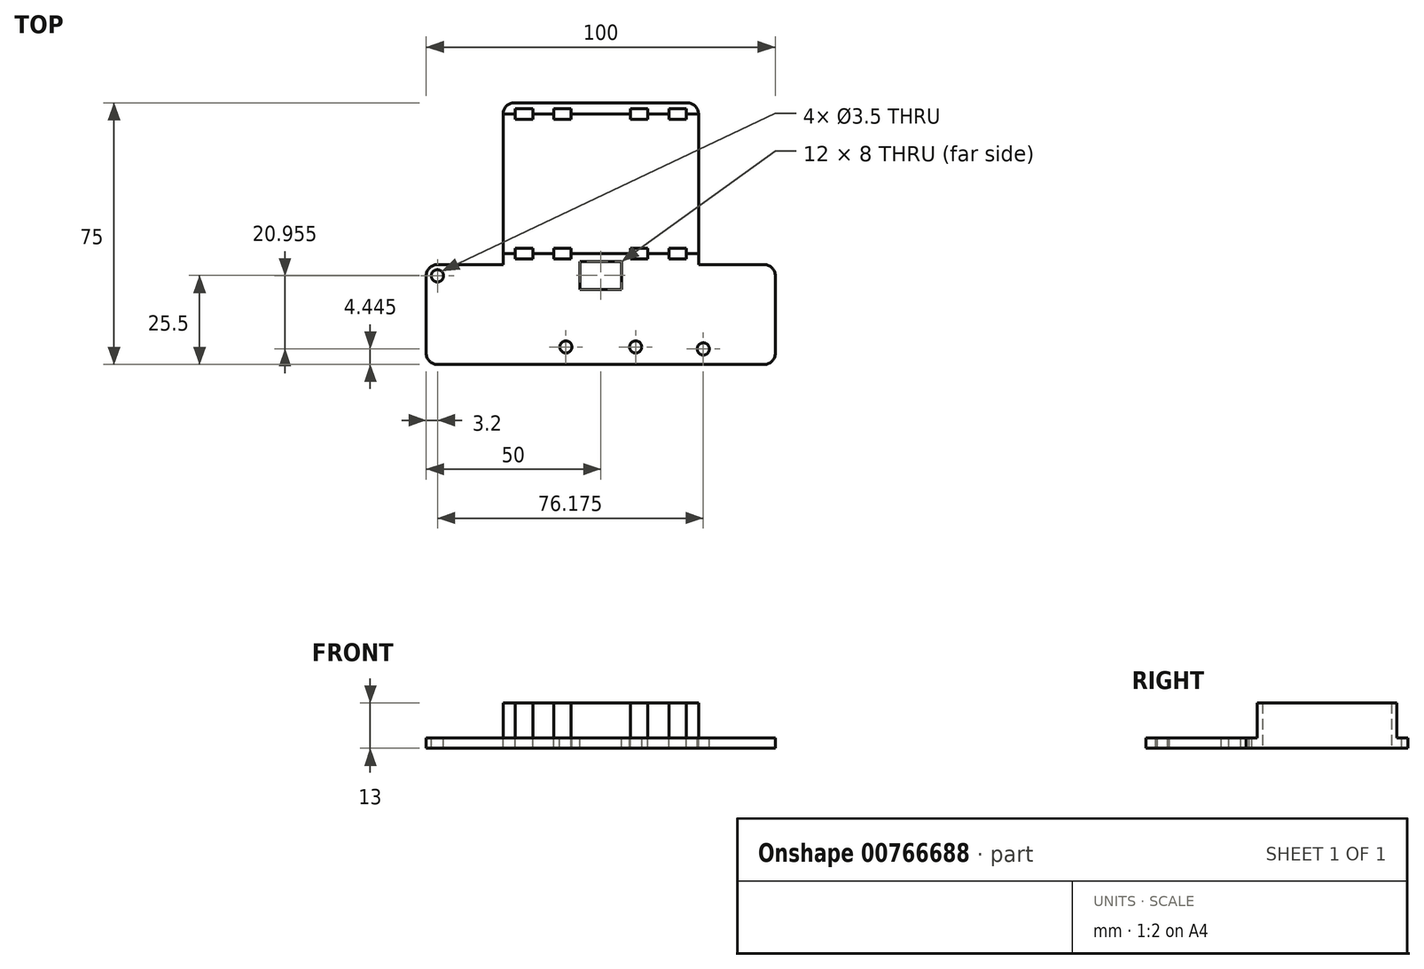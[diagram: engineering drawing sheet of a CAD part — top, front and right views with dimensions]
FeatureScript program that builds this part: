
annotation { "Feature Type Name" : "Feature", "Feature Type Description" : "" }
export const myFeature = defineFeature(function(context is Context, id is Id, definition is map)
    precondition{}
    {
        {
            var Q0;
            Q0=qCreatedBy(makeId("Top.planeOp"),FACE);
            var sketch = newSketch(context, id + "F0", { "sketchPlane" : qUnion([Q0])});
            skLineSegment(sketch, "E0.bottom", {"start": v(-28, -37.5) * mm, "end": v(0, -37.5) * mm});
            skLineSegment(sketch, "E0.top", {"start": v(-28, 37.5) * mm, "end": v(28, 37.5) * mm});
            skPoint(sketch, "E0.middle", {"position": v(0, 0) * mm});
            skCircle(sketch, "E1", {"center": v(-10, -32.5) * mm, "radius": 1.75 * mm});
            skCircle(sketch, "E2", {"center": v(10, -32.5) * mm, "radius": 1.75 * mm});
            skCircle(sketch, "E3", {"center": v(-46.8, -12.1) * mm, "radius": 1.75 * mm});
            skCircle(sketch, "E4", {"center": v(29.38, -33.05) * mm, "radius": 1.75 * mm});
            skLineSegment(sketch, "E5", {"start": v(-28, -37.5) * mm, "end": v(-50, -37.5) * mm});
            skLineSegment(sketch, "E6", {"start": v(28, -37.5) * mm, "end": v(50, -37.5) * mm});
            skLineSegment(sketch, "E7", {"start": v(50, -37.5) * mm, "end": v(50, -8.9) * mm});
            skLineSegment(sketch, "E8", {"start": v(50, -8.9) * mm, "end": v(-50, -8.9) * mm});
            skLineSegment(sketch, "E9", {"start": v(-50, -8.9) * mm, "end": v(-50, -37.5) * mm});
            skLineSegment(sketch, "E10.trimOffspring", {"start": v(28, -8.9) * mm, "end": v(28, 37.5) * mm});
            skLineSegment(sketch, "E11.trimOffspring", {"start": v(-28, -8.9) * mm, "end": v(-28, 14.3) * mm});
            skLineSegment(sketch, "E12", {"start": v(0, -37.5) * mm, "end": v(28, -37.5) * mm});
            skLineSegment(sketch, "E13", {"start": v(-28, 14.3) * mm, "end": v(-28, 37.5) * mm});
            skLineSegment(sketch, "E14", {"start": v(-28, 34.3) * mm, "end": v(28, 34.3) * mm});
            skLineSegment(sketch, "E15", {"start": v(-28, -5.7) * mm, "end": v(28, -5.7) * mm});
            skLineSegment(sketch, "E16", {"start": v(-5, -5.7) * mm, "end": v(-5, 34.3) * mm});
            skLineSegment(sketch, "E17", {"start": v(5, 34.3) * mm, "end": v(5, -5.7) * mm});
            skLineSegment(sketch, "E18.bottom", {"start": v(-19.5, 35.8) * mm, "end": v(-24.5, 35.8) * mm});
            skLineSegment(sketch, "E18.top", {"start": v(-19.5, 32.8) * mm, "end": v(-24.5, 32.8) * mm});
            skLineSegment(sketch, "E18.left", {"start": v(-19.5, 35.8) * mm, "end": v(-19.5, 32.8) * mm});
            skLineSegment(sketch, "E18.right", {"start": v(-24.5, 35.8) * mm, "end": v(-24.5, 32.8) * mm});
            skPoint(sketch, "E18.middle", {"position": v(-22, 34.3) * mm});
            skLineSegment(sketch, "E19.bottom", {"start": v(-13.5, 32.8) * mm, "end": v(-8.5, 32.8) * mm});
            skLineSegment(sketch, "E19.top", {"start": v(-13.5, 35.8) * mm, "end": v(-8.5, 35.8) * mm});
            skLineSegment(sketch, "E19.left", {"start": v(-13.5, 32.8) * mm, "end": v(-13.5, 35.8) * mm});
            skLineSegment(sketch, "E19.right", {"start": v(-8.5, 32.8) * mm, "end": v(-8.5, 35.8) * mm});
            skPoint(sketch, "E19.middle", {"position": v(-11, 34.3) * mm});
            skLineSegment(sketch, "E20.bottom", {"start": v(-19.5, -4.2) * mm, "end": v(-24.5, -4.2) * mm});
            skLineSegment(sketch, "E20.top", {"start": v(-19.5, -7.2) * mm, "end": v(-24.5, -7.2) * mm});
            skLineSegment(sketch, "E20.left", {"start": v(-19.5, -4.2) * mm, "end": v(-19.5, -7.2) * mm});
            skLineSegment(sketch, "E20.right", {"start": v(-24.5, -4.2) * mm, "end": v(-24.5, -7.2) * mm});
            skPoint(sketch, "E20.middle", {"position": v(-22, -5.7) * mm});
            skLineSegment(sketch, "E21.bottom", {"start": v(-13.5, -4.2) * mm, "end": v(-8.5, -4.2) * mm});
            skLineSegment(sketch, "E21.top", {"start": v(-13.5, -7.2) * mm, "end": v(-8.5, -7.2) * mm});
            skLineSegment(sketch, "E21.left", {"start": v(-13.5, -4.2) * mm, "end": v(-13.5, -7.2) * mm});
            skLineSegment(sketch, "E21.right", {"start": v(-8.5, -4.2) * mm, "end": v(-8.5, -7.2) * mm});
            skPoint(sketch, "E21.middle", {"position": v(-11, -5.7) * mm});
            skLineSegment(sketch, "E22.bottom", {"start": v(8.5, 32.8) * mm, "end": v(13.5, 32.8) * mm});
            skLineSegment(sketch, "E22.top", {"start": v(8.5, 35.8) * mm, "end": v(13.5, 35.8) * mm});
            skLineSegment(sketch, "E22.left", {"start": v(8.5, 32.8) * mm, "end": v(8.5, 35.8) * mm});
            skLineSegment(sketch, "E22.right", {"start": v(13.5, 32.8) * mm, "end": v(13.5, 35.8) * mm});
            skPoint(sketch, "E22.middle", {"position": v(11, 34.3) * mm});
            skLineSegment(sketch, "E23.bottom", {"start": v(19.5, 32.8) * mm, "end": v(24.5, 32.8) * mm});
            skLineSegment(sketch, "E23.top", {"start": v(19.5, 35.8) * mm, "end": v(24.5, 35.8) * mm});
            skLineSegment(sketch, "E23.left", {"start": v(19.5, 32.8) * mm, "end": v(19.5, 35.8) * mm});
            skLineSegment(sketch, "E23.right", {"start": v(24.5, 32.8) * mm, "end": v(24.5, 35.8) * mm});
            skPoint(sketch, "E23.middle", {"position": v(22, 34.3) * mm});
            skLineSegment(sketch, "E24.bottom", {"start": v(13.5, -4.2) * mm, "end": v(8.5, -4.2) * mm});
            skLineSegment(sketch, "E24.top", {"start": v(13.5, -7.2) * mm, "end": v(8.5, -7.2) * mm});
            skLineSegment(sketch, "E24.left", {"start": v(13.5, -4.2) * mm, "end": v(13.5, -7.2) * mm});
            skLineSegment(sketch, "E24.right", {"start": v(8.5, -4.2) * mm, "end": v(8.5, -7.2) * mm});
            skPoint(sketch, "E24.middle", {"position": v(11, -5.7) * mm});
            skPoint(sketch, "E24.middle.positionSnap0", {"position": v(11, 32.8) * mm});
            skPoint(sketch, "E24.centerSnap0", {"position": v(11, 32.8) * mm});
            skLineSegment(sketch, "E25.bottom", {"start": v(19.5, -4.2) * mm, "end": v(24.5, -4.2) * mm});
            skLineSegment(sketch, "E25.top", {"start": v(19.5, -7.2) * mm, "end": v(24.5, -7.2) * mm});
            skLineSegment(sketch, "E25.left", {"start": v(19.5, -4.2) * mm, "end": v(19.5, -7.2) * mm});
            skLineSegment(sketch, "E25.right", {"start": v(24.5, -4.2) * mm, "end": v(24.5, -7.2) * mm});
            skPoint(sketch, "E25.middle", {"position": v(22, -5.7) * mm});
            skPoint(sketch, "E25.middle.positionSnap0", {"position": v(22, 32.8) * mm});
            skPoint(sketch, "E25.centerSnap0", {"position": v(22, 32.8) * mm});
            skLineSegment(sketch, "E26.bottom", {"start": v(6, -8) * mm, "end": v(-6, -8) * mm});
            skLineSegment(sketch, "E26.top", {"start": v(6, -16) * mm, "end": v(-6, -16) * mm});
            skLineSegment(sketch, "E26.left", {"start": v(6, -8) * mm, "end": v(6, -16) * mm});
            skLineSegment(sketch, "E26.right", {"start": v(-6, -8) * mm, "end": v(-6, -16) * mm});
            skPoint(sketch, "E26.middle", {"position": v(0, -12) * mm});
            skSolve(sketch);
        }
        {
            var Q0;
            {var subQ0=sQuery(id+"F0.wireOp",EDGE,"E16");Q0=makeQuery(id+"F0.imprint","IMPRINT",FACE,{"disambiguationData":[TD([[makeQuery(id+"F0.imprint","IMPRINT",EDGE,{"derivedFrom":subQ0}),-1.0]])]});}
            var Q1;
            {var subQ3=sQuery(id+"F0.wireOp",EDGE,"E16");Q1=makeQuery(id+"F0.imprint","IMPRINT",FACE,{"disambiguationData":[TD([[makeQuery(id+"F0.imprint","IMPRINT",EDGE,{"derivedFrom":subQ3}),1.0]])]});}
            var Q2;
            {var subQ5=sQuery(id+"F0.wireOp",EDGE,"E17");Q2=makeQuery(id+"F0.imprint","IMPRINT",FACE,{"disambiguationData":[TD([[makeQuery(id+"F0.imprint","IMPRINT",EDGE,{"derivedFrom":subQ5}),1.0]])]});}
            extrude(context, id + "F1", {"entities" : qUnion([Q0, Q1, Q2]), "depth" : 3 * mm, "offsetDistance" : 25 * mm});
        }
        {
            var Q0;
            {var subQ3=sQuery(id+"F0.wireOp",EDGE,"E16");Q0=makeQuery(id+"F0.imprint","IMPRINT",FACE,{"disambiguationData":[TD([[makeQuery(id+"F0.imprint","IMPRINT",EDGE,{"derivedFrom":subQ3}),1.0]])]});}
            var Q1;
            {var subQ5=sQuery(id+"F0.wireOp",EDGE,"E17");Q1=makeQuery(id+"F0.imprint","IMPRINT",FACE,{"disambiguationData":[TD([[makeQuery(id+"F0.imprint","IMPRINT",EDGE,{"derivedFrom":subQ5}),1.0]])]});}
            extrude(context, id + "F2", {"entities" : qUnion([Q0, Q1]), "operationType" : NewBodyOperationType.ADD, "oppositeDirection" : true, "depth" : 10 * mm, "offsetDistance" : 25 * mm});
        }
        {
            var Q0;
            {var subQ0=sQuery(id+"F0.wireOp",EDGE,"E10.trimOffspring");Q0=makeQuery(id+"F2.boolean.opBoolean","MERGE",FACE,{"derivedFrom":[makeQuery(id+"F1.opExtrude","SWEPT_FACE",FACE,{"disambiguationData":[OSD([subQ0])]}),makeQuery(id+"F2.opExtrude","SWEPT_FACE",FACE,{"disambiguationData":[OSD([subQ0])]})]});}
            var sketch = newSketch(context, id + "F3", { "sketchPlane" : qUnion([Q0])});
            skPoint(sketch, "E27.0", {"position": v(14.3, 0) * mm});
            skCircle(sketch, "E28", {"center": v(14.3, -17.5) * mm, "radius": 17.5 * mm});
            skSolve(sketch);
        }
        {
            var Q0;
            {var subQ0=sQuery(id+"F3.wireOp",EDGE,"E28");var subQ1=makeQuery(id+"F2.opExtrude","CAP_EDGE",EDGE,{"disambiguationData":[OSD([sQuery(id+"F0.wireOp",EDGE,"E10.trimOffspring")])],"isStart":false});var subQ2=makeQuery(id+"F3.imprint","INTERSECT",VERTEX,{"disambiguationData":[OD(0.0)],"derivedFrom":[subQ1,subQ0]});Q0=makeQuery(id+"F3.imprint","IMPRINT",FACE,{"disambiguationData":[TD([[makeQuery(id+"F3.imprint","IMPRINT",EDGE,{"disambiguationData":[TD([[subQ2,-1.0]])],"derivedFrom":subQ0}),1.0]])]});}
            var Q1;
            {var subQ0=sQuery(id+"F0.wireOp",EDGE,"E13");var subQ1=sQuery(id+"F0.wireOp",EDGE,"E11.trimOffspring");Q1=makeQuery(id+"F2.boolean.opBoolean","MERGE",FACE,{"derivedFrom":[makeQuery(id+"F1.opExtrude","SWEPT_FACE",FACE,{"disambiguationData":[OSD([subQ1,subQ0])]}),makeQuery(id+"F2.opExtrude","SWEPT_FACE",FACE,{"disambiguationData":[OSD([subQ1,subQ0])]})]});}
            extrude(context, id + "F4", {"entities" : qUnion([Q0]), "operationType" : NewBodyOperationType.REMOVE, "endBound" : BoundingType.UP_TO_SURFACE, "oppositeDirection" : true, "depth" : 25 * mm, "endBoundEntityFace" : qUnion([Q1]), "offsetDistance" : 25 * mm});
        }
        {
            var Q0;
            {var subQ0=sQuery(id+"F0.wireOp",EDGE,"E16");Q0=makeQuery(id+"F0.imprint","IMPRINT",FACE,{"disambiguationData":[TD([[makeQuery(id+"F0.imprint","IMPRINT",EDGE,{"derivedFrom":subQ0}),-1.0]])]});}
            var Q1;
            {var subQ0=sQuery(id+"F0.wireOp",EDGE,"E17");var subQ1=sQuery(id+"F0.wireOp",EDGE,"E10.trimOffspring");var subQ2=sQuery(id+"F0.wireOp",EDGE,"E14");Q1=makeQuery(id+"F4.boolean.opBoolean","SPLIT",FACE,{"disambiguationData":[TD([makeQuery(id+"F2.opExtrude","SWEPT_FACE",FACE,{"disambiguationData":[OSD([subQ2]),TDD([makeQuery(id+"F0.imprint","IMPRINT",EDGE,{"disambiguationData":[TD([[makeQuery(id+"F0.imprint","INTERSECT",VERTEX,{"derivedFrom":[subQ1,subQ2]}),1.0]])],"derivedFrom":subQ2})])]})])],"derivedFrom":makeQuery(id+"F2.opExtrude","CAP_FACE",FACE,{"disambiguationData":[OSD([subQ1,subQ2,sQuery(id+"F0.wireOp",EDGE,"E15"),subQ0])],"isStart":false})});}
            extrude(context, id + "F5", {"entities" : qUnion([Q0]), "operationType" : NewBodyOperationType.ADD, "endBound" : BoundingType.UP_TO_SURFACE, "oppositeDirection" : true, "depth" : 25 * mm, "endBoundEntityFace" : qUnion([Q1]), "offsetDistance" : 25 * mm});
        }
        {
            var Q0;
            {var subQ16=sQuery(id+"F0.wireOp",EDGE,"E0.top");Q0=makeQuery(id+"F0.imprint","IMPRINT",FACE,{"disambiguationData":[TD([[makeQuery(id+"F0.imprint","IMPRINT",EDGE,{"derivedFrom":subQ16}),-1.0]])]});}
            var Q1;
            {var subQ16=sQuery(id+"F0.wireOp",EDGE,"E20.top");Q1=makeQuery(id+"F0.imprint","IMPRINT",FACE,{"disambiguationData":[TD([[makeQuery(id+"F0.imprint","IMPRINT",EDGE,{"derivedFrom":subQ16}),1.0]])]});}
            var Q2;
            Q2=makeQuery(id+"F0.imprint","IMPRINT",FACE,{"disambiguationData":[TD([[makeQuery(id+"F0.imprint","IMPRINT",EDGE,{"derivedFrom":sQuery(id+"F0.wireOp",EDGE,"E0.bottom")}),1.0]])]});
            var Q3;
            {var subQ0=sQuery(id+"F0.wireOp",EDGE,"E17");var subQ1=sQuery(id+"F0.wireOp",EDGE,"E16");var subQ2=sQuery(id+"F0.wireOp",EDGE,"E15");var subQ3=sQuery(id+"F0.wireOp",EDGE,"E14");var subQ5=sQuery(id+"F0.wireOp",EDGE,"E20.left");var subQ6=sQuery(id+"F0.wireOp",EDGE,"E21.left");var subQ8=sQuery(id+"F0.wireOp",EDGE,"E11.trimOffspring");var subQ9=sQuery(id+"F0.wireOp",EDGE,"E20.right");var subQ12=sQuery(id+"F0.wireOp",EDGE,"E24.right");var subQ15=sQuery(id+"F0.wireOp",EDGE,"E21.right");var subQ19=sQuery(id+"F0.wireOp",EDGE,"E20.bottom");var subQ20=sQuery(id+"F0.wireOp",EDGE,"E13");var subQ24=sQuery(id+"F0.wireOp",EDGE,"E21.bottom");var subQ26=sQuery(id+"F0.wireOp",EDGE,"E19.right");var subQ27=sQuery(id+"F0.wireOp",EDGE,"E19.left");var subQ28=sQuery(id+"F0.wireOp",EDGE,"E19.bottom");var subQ29=sQuery(id+"F0.wireOp",EDGE,"E18.right");var subQ30=sQuery(id+"F0.wireOp",EDGE,"E18.left");var subQ31=sQuery(id+"F0.wireOp",EDGE,"E18.top");var subQ32=makeQuery(id+"F2.opExtrude","CAP_FACE",FACE,{"disambiguationData":[OSD([subQ8,subQ20,subQ3,subQ2,subQ1,subQ31,subQ30,subQ29,subQ28,subQ27,subQ26,subQ19,subQ5,subQ9,subQ24,subQ6,subQ15])],"isStart":false});var subQ36=sQuery(id+"F0.wireOp",EDGE,"E22.left");var subQ43=sQuery(id+"F0.wireOp",EDGE,"E25.right");var subQ44=sQuery(id+"F0.wireOp",EDGE,"E10.trimOffspring");var subQ47=sQuery(id+"F0.wireOp",EDGE,"E25.bottom");var subQ48=sQuery(id+"F0.wireOp",EDGE,"E24.left");var subQ49=sQuery(id+"F0.wireOp",EDGE,"E25.left");var subQ52=sQuery(id+"F0.wireOp",EDGE,"E24.bottom");var subQ54=sQuery(id+"F0.wireOp",EDGE,"E23.right");var subQ55=sQuery(id+"F0.wireOp",EDGE,"E23.left");var subQ56=sQuery(id+"F0.wireOp",EDGE,"E23.bottom");var subQ57=sQuery(id+"F0.wireOp",EDGE,"E22.right");var subQ58=sQuery(id+"F0.wireOp",EDGE,"E22.bottom");var subQ59=makeQuery(id+"F2.opExtrude","CAP_FACE",FACE,{"disambiguationData":[OSD([subQ44,subQ3,subQ2,subQ0,subQ58,subQ36,subQ57,subQ56,subQ55,subQ54,subQ52,subQ48,subQ12,subQ47,subQ49,subQ43])],"isStart":false});Q3=makeQuery(id+"F5.boolean.opBoolean","MERGE",FACE,{"derivedFrom":[makeQuery(id+"F4.boolean.opBoolean","SPLIT",FACE,{"disambiguationData":[TD([makeQuery(id+"F1.opExtrude","SWEPT_FACE",FACE,{"disambiguationData":[OSD([subQ58])]})])],"derivedFrom":subQ59}),makeQuery(id+"F4.boolean.opBoolean","SPLIT",FACE,{"disambiguationData":[TD([makeQuery(id+"F1.opExtrude","SWEPT_FACE",FACE,{"disambiguationData":[OSD([subQ52])]})])],"derivedFrom":subQ59}),makeQuery(id+"F4.boolean.opBoolean","SPLIT",FACE,{"disambiguationData":[TD([makeQuery(id+"F1.opExtrude","SWEPT_FACE",FACE,{"disambiguationData":[OSD([subQ31])]})])],"derivedFrom":subQ32}),makeQuery(id+"F4.boolean.opBoolean","SPLIT",FACE,{"disambiguationData":[TD([makeQuery(id+"F1.opExtrude","SWEPT_FACE",FACE,{"disambiguationData":[OSD([subQ19])]})])],"derivedFrom":subQ32}),makeQuery(id+"F5.opExtrude","CAP_FACE",FACE,{"disambiguationData":[OSD([subQ3,subQ2,subQ1,subQ0])],"isStart":false})]});}
            var Q4;
            {var subQ0=sQuery(id+"F0.wireOp",EDGE,"E17");var subQ1=sQuery(id+"F0.wireOp",EDGE,"E16");var subQ2=sQuery(id+"F0.wireOp",EDGE,"E15");var subQ3=sQuery(id+"F0.wireOp",EDGE,"E14");var subQ5=sQuery(id+"F0.wireOp",EDGE,"E20.left");var subQ6=sQuery(id+"F0.wireOp",EDGE,"E21.left");var subQ8=sQuery(id+"F0.wireOp",EDGE,"E11.trimOffspring");var subQ9=sQuery(id+"F0.wireOp",EDGE,"E20.right");var subQ12=sQuery(id+"F0.wireOp",EDGE,"E24.right");var subQ15=sQuery(id+"F0.wireOp",EDGE,"E21.right");var subQ19=sQuery(id+"F0.wireOp",EDGE,"E20.bottom");var subQ20=sQuery(id+"F0.wireOp",EDGE,"E13");var subQ24=sQuery(id+"F0.wireOp",EDGE,"E21.bottom");var subQ26=sQuery(id+"F0.wireOp",EDGE,"E19.right");var subQ27=sQuery(id+"F0.wireOp",EDGE,"E19.left");var subQ28=sQuery(id+"F0.wireOp",EDGE,"E19.bottom");var subQ29=sQuery(id+"F0.wireOp",EDGE,"E18.right");var subQ30=sQuery(id+"F0.wireOp",EDGE,"E18.left");var subQ31=sQuery(id+"F0.wireOp",EDGE,"E18.top");var subQ32=makeQuery(id+"F2.opExtrude","CAP_FACE",FACE,{"disambiguationData":[OSD([subQ8,subQ20,subQ3,subQ2,subQ1,subQ31,subQ30,subQ29,subQ28,subQ27,subQ26,subQ19,subQ5,subQ9,subQ24,subQ6,subQ15])],"isStart":false});var subQ36=sQuery(id+"F0.wireOp",EDGE,"E22.left");var subQ43=sQuery(id+"F0.wireOp",EDGE,"E25.right");var subQ44=sQuery(id+"F0.wireOp",EDGE,"E10.trimOffspring");var subQ47=sQuery(id+"F0.wireOp",EDGE,"E25.bottom");var subQ48=sQuery(id+"F0.wireOp",EDGE,"E24.left");var subQ49=sQuery(id+"F0.wireOp",EDGE,"E25.left");var subQ52=sQuery(id+"F0.wireOp",EDGE,"E24.bottom");var subQ54=sQuery(id+"F0.wireOp",EDGE,"E23.right");var subQ55=sQuery(id+"F0.wireOp",EDGE,"E23.left");var subQ56=sQuery(id+"F0.wireOp",EDGE,"E23.bottom");var subQ57=sQuery(id+"F0.wireOp",EDGE,"E22.right");var subQ58=sQuery(id+"F0.wireOp",EDGE,"E22.bottom");var subQ59=makeQuery(id+"F2.opExtrude","CAP_FACE",FACE,{"disambiguationData":[OSD([subQ44,subQ3,subQ2,subQ0,subQ58,subQ36,subQ57,subQ56,subQ55,subQ54,subQ52,subQ48,subQ12,subQ47,subQ49,subQ43])],"isStart":false});Q4=makeQuery(id+"F5.boolean.opBoolean","MERGE",FACE,{"derivedFrom":[makeQuery(id+"F4.boolean.opBoolean","SPLIT",FACE,{"disambiguationData":[TD([makeQuery(id+"F1.opExtrude","SWEPT_FACE",FACE,{"disambiguationData":[OSD([subQ58])]})])],"derivedFrom":subQ59}),makeQuery(id+"F4.boolean.opBoolean","SPLIT",FACE,{"disambiguationData":[TD([makeQuery(id+"F1.opExtrude","SWEPT_FACE",FACE,{"disambiguationData":[OSD([subQ52])]})])],"derivedFrom":subQ59}),makeQuery(id+"F4.boolean.opBoolean","SPLIT",FACE,{"disambiguationData":[TD([makeQuery(id+"F1.opExtrude","SWEPT_FACE",FACE,{"disambiguationData":[OSD([subQ31])]})])],"derivedFrom":subQ32}),makeQuery(id+"F4.boolean.opBoolean","SPLIT",FACE,{"disambiguationData":[TD([makeQuery(id+"F1.opExtrude","SWEPT_FACE",FACE,{"disambiguationData":[OSD([subQ19])]})])],"derivedFrom":subQ32}),makeQuery(id+"F5.opExtrude","CAP_FACE",FACE,{"disambiguationData":[OSD([subQ3,subQ2,subQ1,subQ0])],"isStart":false})]});}
            extrude(context, id + "F6", {"entities" : qUnion([Q0, Q1, Q2]), "operationType" : NewBodyOperationType.ADD, "endBound" : BoundingType.UP_TO_SURFACE, "oppositeDirection" : true, "depth" : 10.8 * mm, "endBoundEntityFace" : qUnion([Q3]), "offsetDistance" : 25 * mm, "hasSecondDirection" : true, "secondDirectionOppositeDirection" : true, "secondDirectionDepth" : 7 * mm, "secondDirectionBoundEntityFace" : qUnion([Q4])});
        }
        {
            var Q0;
            Q0=makeQuery(id+"F6.opExtrude","SWEPT_EDGE",EDGE,{"disambiguationData":[OSD([sQuery(id+"F0.wireOp",EDGE,"E0.top"),sQuery(id+"F0.wireOp",EDGE,"E10.trimOffspring")])]});
            var Q1;
            Q1=makeQuery(id+"F6.opExtrude","SWEPT_EDGE",EDGE,{"disambiguationData":[OSD([sQuery(id+"F0.wireOp",EDGE,"E0.top"),sQuery(id+"F0.wireOp",EDGE,"E13")])]});
            var Q2;
            Q2=makeQuery(id+"F6.opExtrude","SWEPT_EDGE",EDGE,{"disambiguationData":[OSD([sQuery(id+"F0.wireOp",EDGE,"E7"),sQuery(id+"F0.wireOp",EDGE,"E8")])]});
            var Q3;
            Q3=makeQuery(id+"F6.opExtrude","SWEPT_EDGE",EDGE,{"disambiguationData":[OSD([sQuery(id+"F0.wireOp",EDGE,"E6"),sQuery(id+"F0.wireOp",EDGE,"E7")])]});
            var Q4;
            Q4=makeQuery(id+"F6.opExtrude","SWEPT_EDGE",EDGE,{"disambiguationData":[OSD([sQuery(id+"F0.wireOp",EDGE,"E5"),sQuery(id+"F0.wireOp",EDGE,"E9")])]});
            var Q5;
            Q5=makeQuery(id+"F6.opExtrude","SWEPT_EDGE",EDGE,{"disambiguationData":[OSD([sQuery(id+"F0.wireOp",EDGE,"E8"),sQuery(id+"F0.wireOp",EDGE,"E9")])]});
            fillet(context, id + "F7", {"entities" : qUnion([Q0, Q1, Q2, Q3, Q4, Q5]), "radius" : 3.2 * mm, "tangentPropagation" : true, "allowEdgeOverflow" : false});
        }
    });
